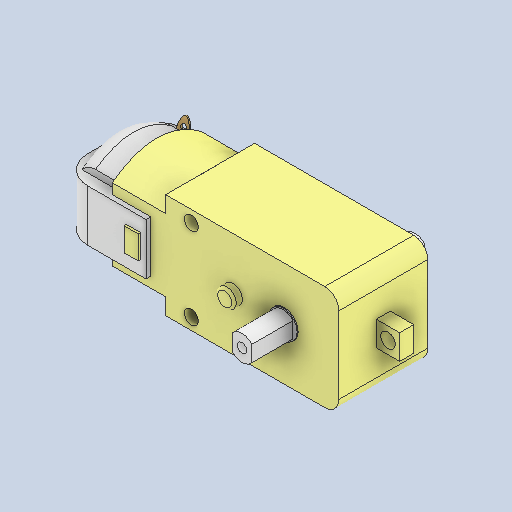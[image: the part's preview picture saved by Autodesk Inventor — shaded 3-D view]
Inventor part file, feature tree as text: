
AUTODESK INVENTOR PART (.ipt)
format: ipt  version: 2023.1 (Build 271208000, 208)  size: 264,192 bytes
history: mixed  units: in
note: dims shown in document units (in); Inventor stores cm internally (conversion verified against a paired STEP export)
features: other x2, mirror x1, imported_body x1
ambient origin geometry x8: Origin, YZ Plane, XZ Plane, XY Plane, X Axis, Y Axis, Z Axis, Center Point
bodies: Body1 (imported_parasolid)
feature tree (4):
  other  "Sólido1"
  other  "Plano1"
  mirror  "Simetría2"
  imported_body  NMx_Import_Brep_tag  [imported B-rep: ~5 faces, bbox_mm=None]
